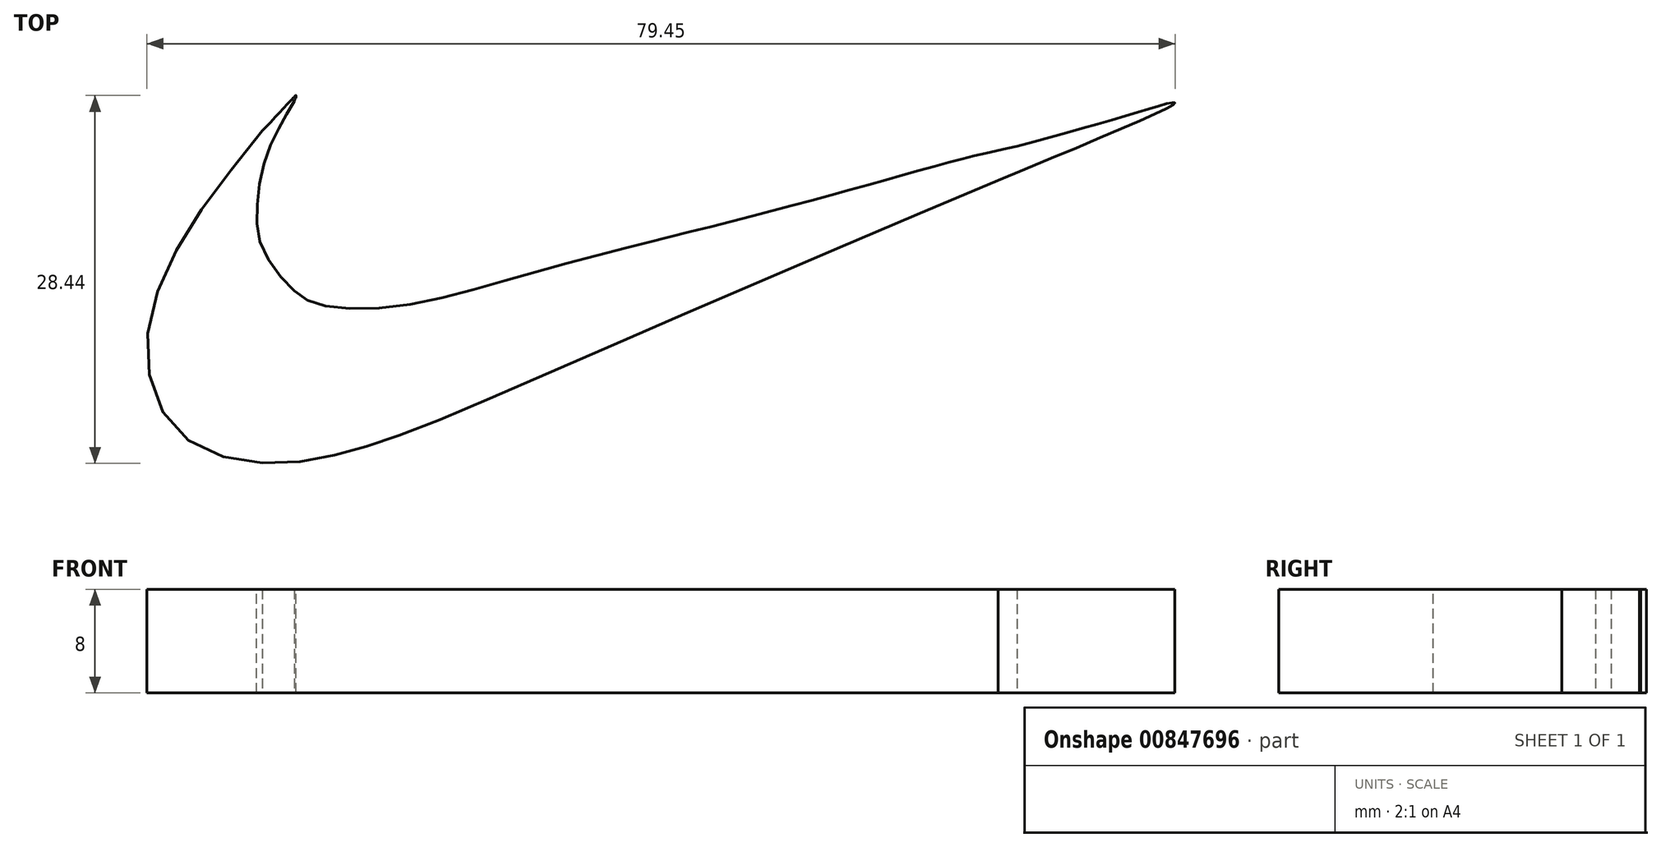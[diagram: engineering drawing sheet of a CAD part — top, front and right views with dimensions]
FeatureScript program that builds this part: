
annotation { "Feature Type Name" : "Feature", "Feature Type Description" : "" }
export const myFeature = defineFeature(function(context is Context, id is Id, definition is map)
    precondition{}
    {
        {
            var Q0;
            Q0=qCreatedBy(makeId("Top.planeOp"),FACE);
            var sketch = newSketch(context, id + "F0", { "sketchPlane" : qUnion([Q0])});
            skFitSpline(sketch, "E0", {"points": [v(-31.93, 42.1) * mm, v(-32.98, 40.27) * mm, v(-34.23, 37.38) * mm, v(-34.81, 33.7) * mm, v(-34.4, 30.74) * mm, v(-32.21, 27.7) * mm, v(-30.09, 26.4) * mm, v(-23.66, 26.29) * mm, v(-14.64, 28.52) * mm, v(-6.22, 30.77) * mm], "startDerivative": vector(-13.34, -22.64) * mm, "endDerivative": vector(53.4, 13.78) * mm});
            skFitSpline(sketch, "E1", {"points": [v(-6.22, 30.77) * mm, v(9.2, 34.75) * mm, v(19.4, 37.57) * mm, v(23.94, 38.61) * mm], "startDerivative": vector(37.5, 9.4) * mm, "endDerivative": vector(18, 3.82) * mm});
            skFitSpline(sketch, "E2", {"points": [v(23.94, 38.61) * mm, v(33.08, 41.2) * mm, v(35.97, 42) * mm, v(36.14, 41.96) * mm, v(22.46, 36) * mm], "startDerivative": vector(29.7, 8.2) * mm, "endDerivative": vector(-48.04, -19.82) * mm});
            skFitSpline(sketch, "E3", {"points": [v(22.46, 36) * mm, v(-7.24, 23.28) * mm, v(-22.71, 16.67) * mm, v(-28.08, 14.92) * mm, v(-33.94, 14.11) * mm, v(-40.5, 16.17) * mm, v(-43.3, 22.4) * mm, v(-40.93, 30.77) * mm, v(-34.38, 39.81) * mm], "startDerivative": vector(-144.2, -61.26) * mm, "endDerivative": vector(56.65, 69.51) * mm});
            skFitSpline(sketch, "E4", {"points": [v(-34.38, 39.81) * mm, v(-32.08, 42.29) * mm, v(-31.78, 42.55) * mm, v(-31.93, 42.1) * mm], "startDerivative": vector(4.7, 5.05) * mm, "endDerivative": vector(-1.14, -2.86) * mm});
            skSolve(sketch);
        }
        {
            var Q0;
            Q0=qSketchRegion(id+"F0",true);
            extrude(context, id + "F1", {"entities" : qUnion([Q0]), "depth" : 8 * mm, "offsetDistance" : 25.4 * mm});
        }
    });
